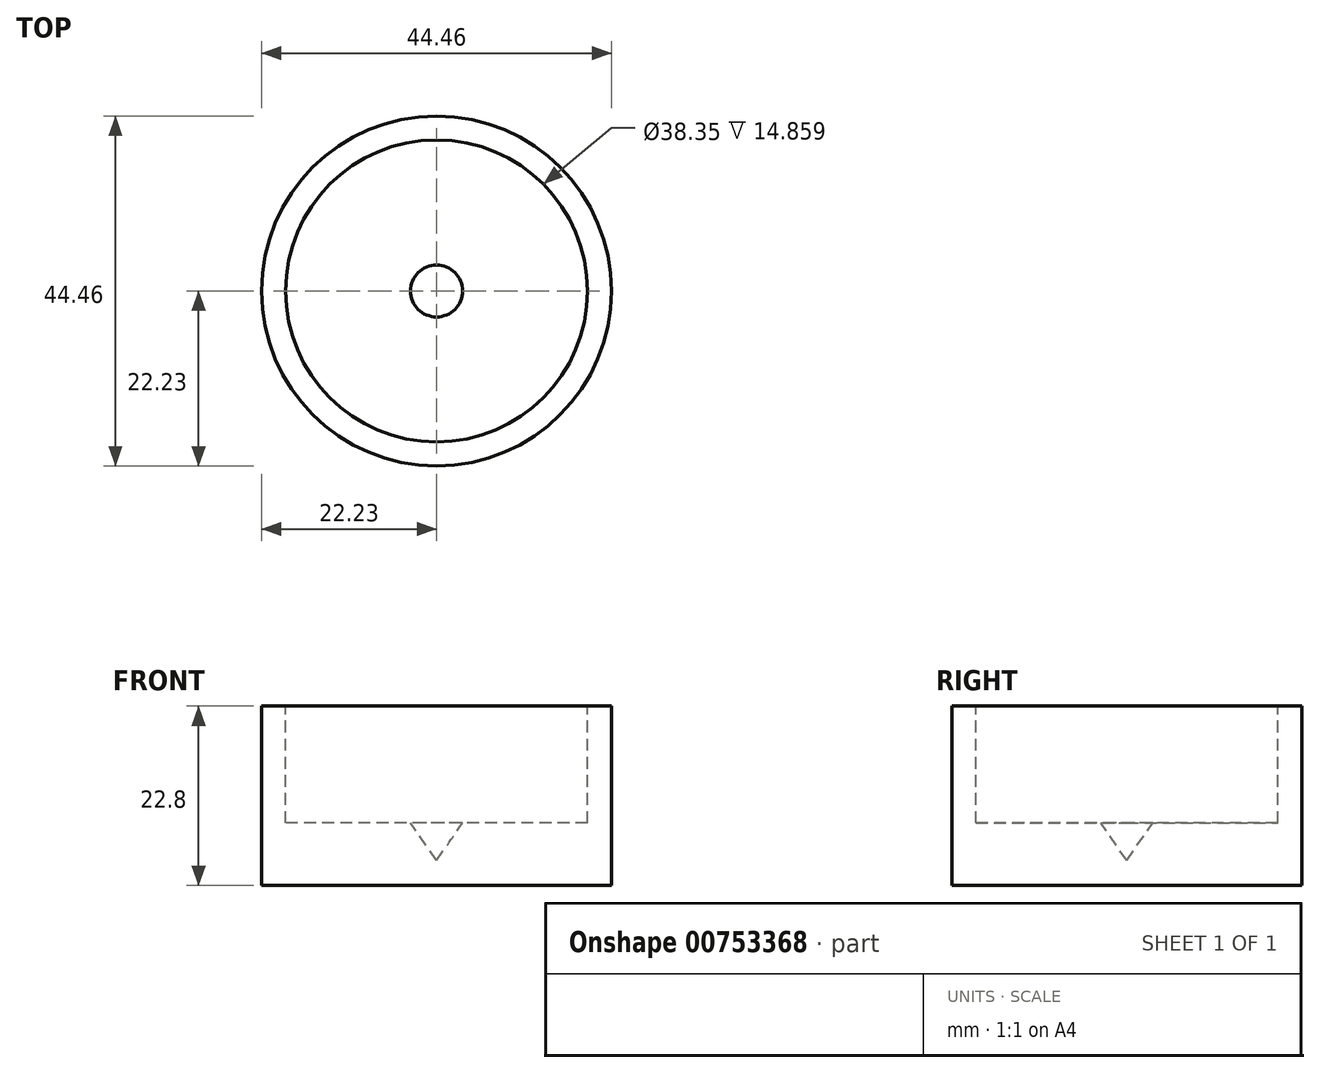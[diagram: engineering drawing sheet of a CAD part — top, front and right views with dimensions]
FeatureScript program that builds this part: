
annotation { "Feature Type Name" : "Feature", "Feature Type Description" : "" }
export const myFeature = defineFeature(function(context is Context, id is Id, definition is map)
    precondition{}
    {
        {
            var Q0;
            Q0=qCreatedBy(makeId("Front.planeOp"),FACE);
            var sketch = newSketch(context, id + "F0", { "sketchPlane" : qUnion([Q0])});
            skLineSegment(sketch, "E0", {"start": v(0, 20.31) * mm, "end": v(0, -16.45) * mm, "construction": true});
            skLineSegment(sketch, "E1", {"start": v(0, 0) * mm, "end": v(3.3, 4.76) * mm});
            skLineSegment(sketch, "E2", {"start": v(3.3, 4.76) * mm, "end": v(19.18, 4.76) * mm});
            skLineSegment(sketch, "E3", {"start": v(19.18, 4.76) * mm, "end": v(19.18, 19.62) * mm});
            skLineSegment(sketch, "E4", {"start": v(19.18, 19.62) * mm, "end": v(22.23, 19.62) * mm});
            skLineSegment(sketch, "E5", {"start": v(22.23, 19.62) * mm, "end": v(22.23, 0) * mm});
            skLineSegment(sketch, "E6", {"start": v(22.23, 0) * mm, "end": v(22.23, -3.17) * mm});
            skLineSegment(sketch, "E7", {"start": v(22.23, -3.17) * mm, "end": v(0, -3.18) * mm});
            skLineSegment(sketch, "E8", {"start": v(0, 0) * mm, "end": v(0, -3.18) * mm});
            skSolve(sketch);
        }
        {
            var Q0;
            Q0=makeQuery(id+"F0.imprint","IMPRINT",FACE,{"disambiguationData":[TD([[makeQuery(id+"F0.imprint","IMPRINT",EDGE,{"derivedFrom":sQuery(id+"F0.wireOp",EDGE,"E1")}),-1.0]])]});
            var Q1;
            Q1=sQuery(id+"F0.wireOp",EDGE,"E0");
            revolve(context, id + "F1", {"surfaceOperationType" : NewSurfaceOperationType.NEW, "entities" : qUnion([Q0]), "axis" : qUnion([Q1]), "revolveType" : RevolveType.FULL});
        }
    });
